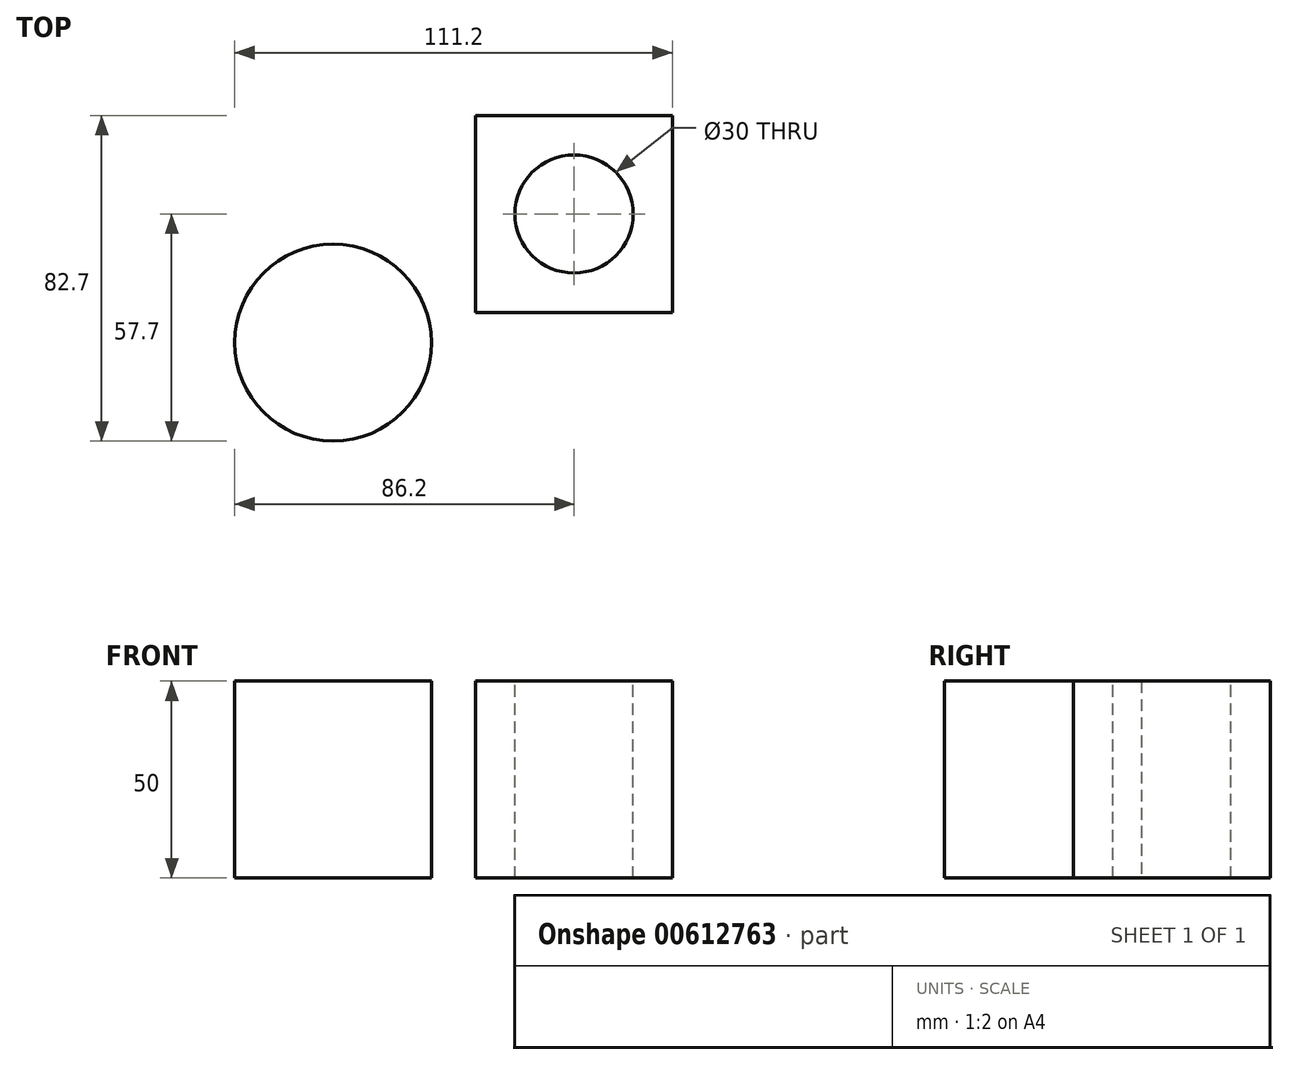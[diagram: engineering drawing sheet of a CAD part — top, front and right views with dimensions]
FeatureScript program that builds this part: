
annotation { "Feature Type Name" : "Feature", "Feature Type Description" : "" }
export const myFeature = defineFeature(function(context is Context, id is Id, definition is map)
    precondition{}
    {
        {
            var Q0;
            Q0=qCreatedBy(makeId("Top.planeOp"),FACE);
            var sketch = newSketch(context, id + "F0", { "sketchPlane" : qUnion([Q0])});
            skLineSegment(sketch, "E0.bottom", {"start": v(-25, 25) * mm, "end": v(25, 25) * mm});
            skLineSegment(sketch, "E0.top", {"start": v(-25, -25) * mm, "end": v(25, -25) * mm});
            skLineSegment(sketch, "E0.left", {"start": v(-25, 25) * mm, "end": v(-25, -25) * mm});
            skLineSegment(sketch, "E0.right", {"start": v(25, 25) * mm, "end": v(25, -25) * mm});
            skPoint(sketch, "E0.middle", {"position": v(0, 0) * mm});
            skSolve(sketch);
        }
        {
            var Q0;
            Q0 = qSketchRegion(id + "F0", true);
            extrude(context, id + "F1", {"entities" : qUnion([Q0]), "depth" : 50 * mm, "offsetDistance" : 25 * mm});
        }
        {
            var Q0;
            Q0=makeQuery(id+"F1.opExtrude","CAP_FACE",FACE,{"disambiguationData":[OSD([sQuery(id+"F0.wireOp",EDGE,"E0.bottom"),sQuery(id+"F0.wireOp",EDGE,"E0.top"),sQuery(id+"F0.wireOp",EDGE,"E0.left"),sQuery(id+"F0.wireOp",EDGE,"E0.right")])],"isStart":false});
            var sketch = newSketch(context, id + "F2", { "sketchPlane" : qUnion([Q0])});
            skCircle(sketch, "E1", {"center": v(0, 0) * mm, "radius": 15 * mm});
            skSolve(sketch);
        }
        {
            var Q0;
            Q0 = qSketchRegion(id + "F2", true);
            extrude(context, id + "F3", {"entities" : qUnion([Q0]), "operationType" : NewBodyOperationType.REMOVE, "oppositeDirection" : true, "depth" : 50 * mm, "offsetDistance" : 25 * mm});
        }
        {
            var Q0;
            Q0=qCreatedBy(makeId("Top.planeOp"),FACE);
            var sketch = newSketch(context, id + "F4", { "sketchPlane" : qUnion([Q0])});
            skCircle(sketch, "E2", {"center": v(-61.2, -32.7) * mm, "radius": 25 * mm});
            skSolve(sketch);
        }
        {
            var Q0;
            Q0 = qSketchRegion(id + "F4", true);
            extrude(context, id + "F5", {"entities" : qUnion([Q0]), "depth" : 50 * mm, "offsetDistance" : 25 * mm});
        }
    });
